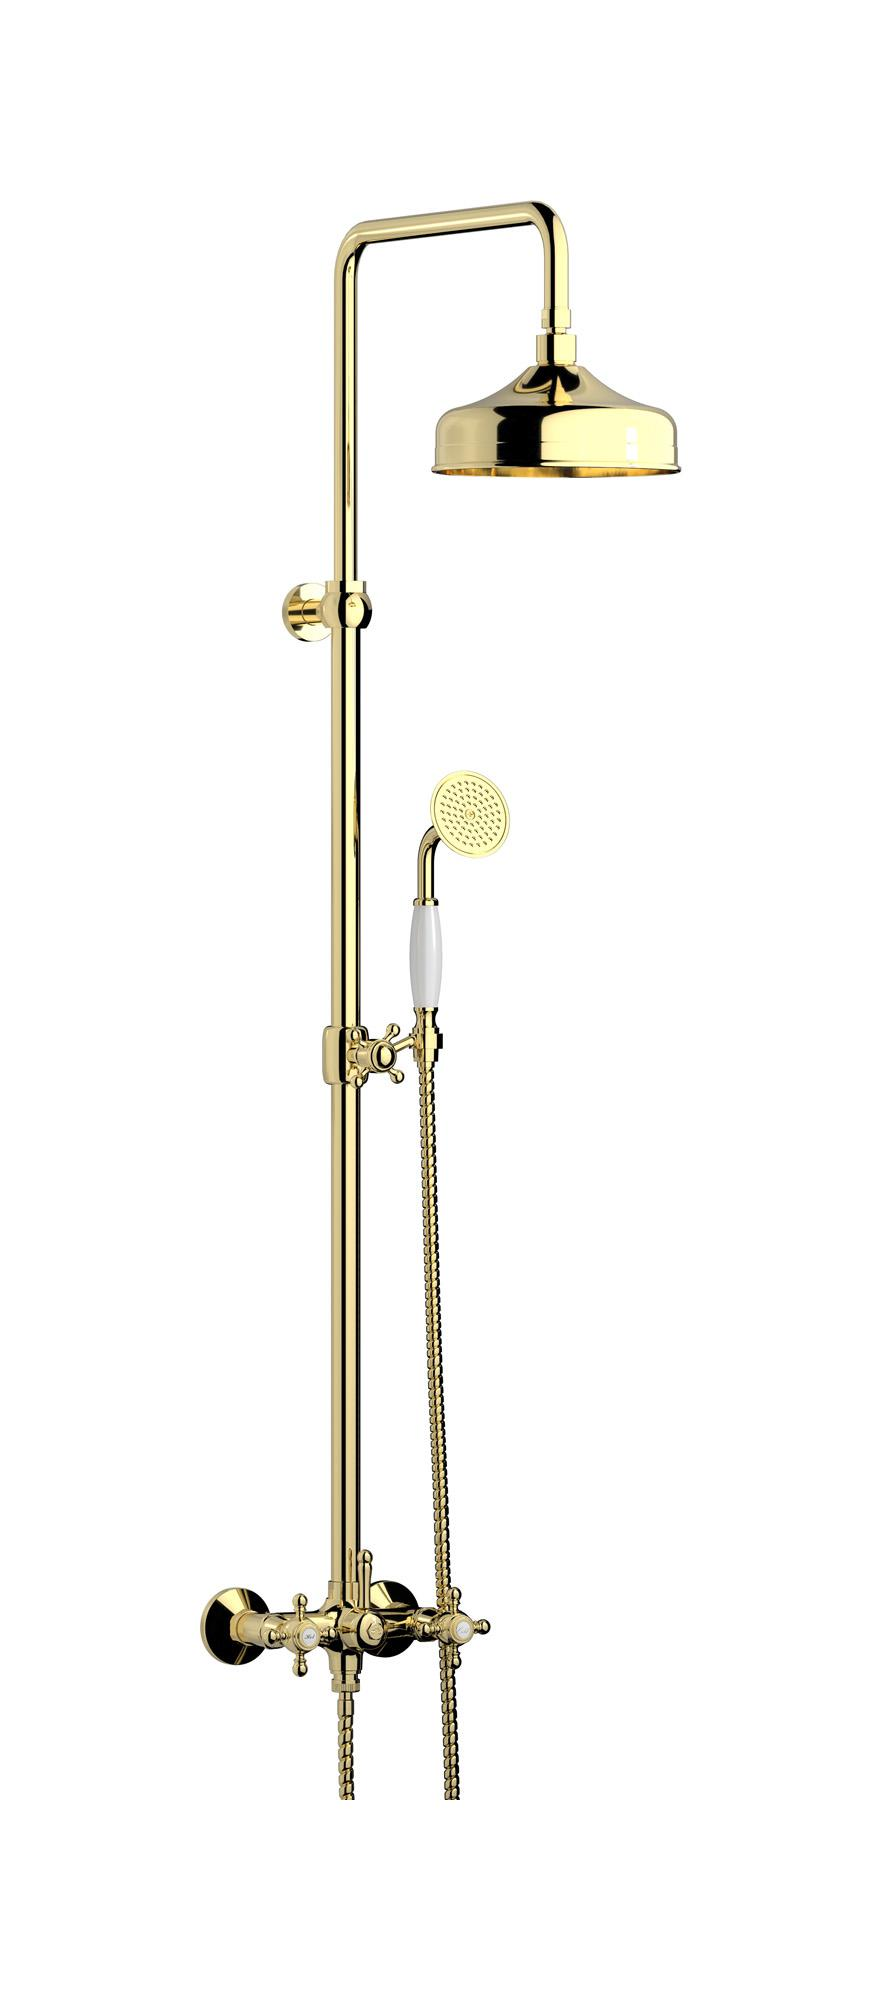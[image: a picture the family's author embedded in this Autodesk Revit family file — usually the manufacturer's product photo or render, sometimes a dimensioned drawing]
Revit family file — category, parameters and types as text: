
# Revit family: HR800
name_source: partatom
category: Apparecchi idraulici
units: mm (PartAtom-declared; Revit-internal decimal feet)

## family parameters
Basato su piano di lavoro = No
Condiviso = No
Mantieni orientamento annotazione = No
Numero OmniClass = 23.45.55.17
Punto di calcolo locali = No
Quota connettore circolare = Usa diametro
Sempre verticale = Sì
Taglio con vuoti quando caricato = No
Tipo di parte = Normale
Titolo OmniClass = Mixing Faucets

## types (8) — shared parameters
Cold water inlet = 10 mm  [stored 0.0328084 ft]
Commenti sul tipo = Thermostatic shower column with shower kit
Connessione CW = No
Connessione HW = No
Connessione di scarico = No
Connessione di ventilazione = No
Descrizione = Thermostatic shower column with shower kit
Hot water inlet = 10 mm  [stored 0.0328084 ft]
Produttore = IB Rubinetterie S.p.A.
URL = https://www.weareib.it
zero-valued in all types: Prospetto di default

## per-type parameters (varying)
| type | Finishes surface | Immagine tipo | Modello |
| Chrome | IB_Chrome | HR800CC.jpg | HR800CC |
| Antique Bronze | IB_Antique bronze | HR800BB.jpg | HR800BB |
| Pale gold | IB_Pale gold | HR800II.jpg | HR800II |
| Brushed gold | IB_brushed gold | HR800OS.jpg | HR800OS |
| Platinum | IB_Platinum | HR800PL.jpg | HR800PL |
| Antique Copper | IB_Antique copper | HR800RR.jpg | HR800RR |
| Rose gold | IB_Rose gold | HR800RS.jpg | HR800RS |
| Brushed nickel | IB_Brushed nickel | HR800SS.jpg | HR800SS |

note: [stored X ft] marks values corroborated as IEEE doubles in the binary element streams (Revit-internal decimal feet)
